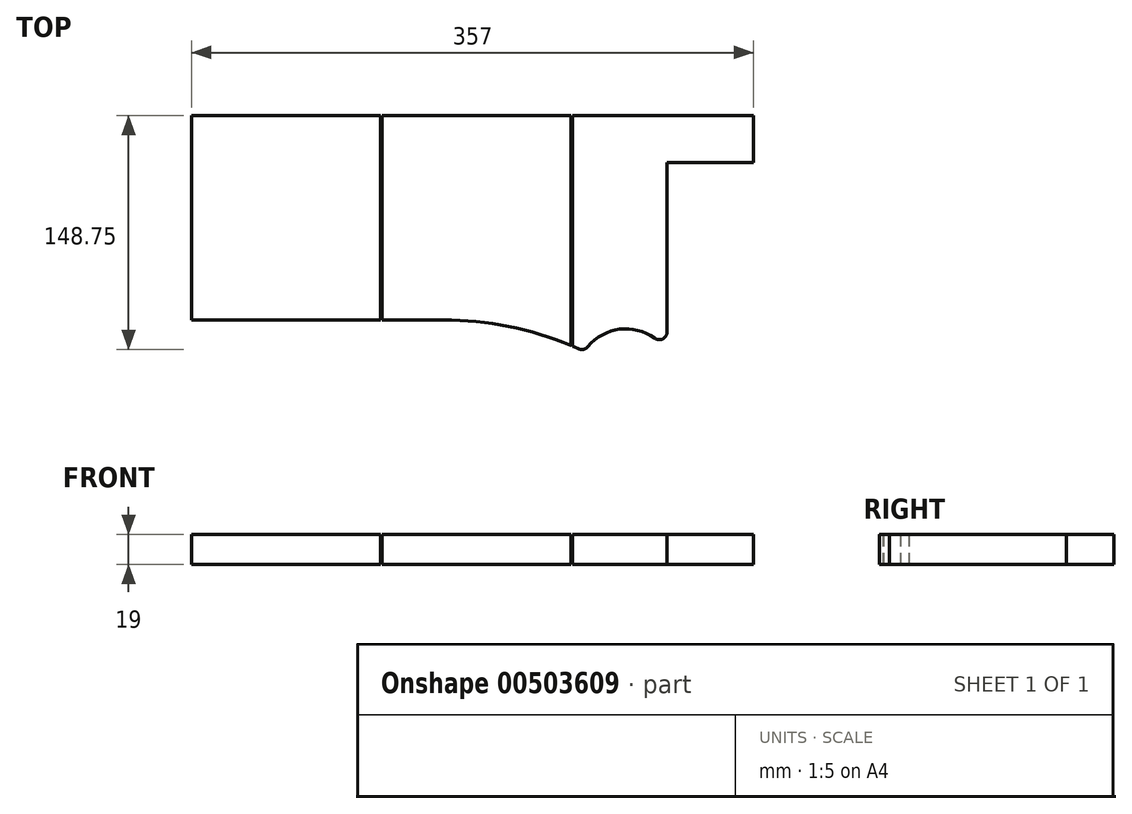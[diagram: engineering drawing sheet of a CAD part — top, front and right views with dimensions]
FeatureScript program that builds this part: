
annotation { "Feature Type Name" : "Feature", "Feature Type Description" : "" }
export const myFeature = defineFeature(function(context is Context, id is Id, definition is map)
    precondition{}
    {
        {
            var Q0;
            Q0=qCreatedBy(makeId("Top.planeOp"),FACE);
            var sketch = newSketch(context, id + "F0", { "sketchPlane" : qUnion([Q0])});
            skLineSegment(sketch, "E0.bottom", {"start": v(-262.8, 99.04) * mm, "end": v(-146.42, 99.04) * mm});
            skLineSegment(sketch, "E0.top", {"start": v(-262.8, -30.96) * mm, "end": v(-102.8, -30.96) * mm});
            skLineSegment(sketch, "E0.left", {"start": v(-262.8, 99.04) * mm, "end": v(-262.8, -30.96) * mm});
            skLineSegment(sketch, "E1", {"start": v(-20.8, -76.9) * mm, "end": v(-21.8, -76.79) * mm});
            skLineSegment(sketch, "E2.trimOffspring", {"start": v(-147.44, 99.04) * mm, "end": v(-40.78, 99.04) * mm});
            skLineSegment(sketch, "E3.bottom", {"start": v(-40.78, 99.04) * mm, "end": v(94.2, 99.04) * mm});
            skLineSegment(sketch, "E3.top", {"start": v(39.2, 69.04) * mm, "end": v(94.2, 69.04) * mm});
            skLineSegment(sketch, "E3.right", {"start": v(94.2, 99.04) * mm, "end": v(94.2, 69.04) * mm});
            skLineSegment(sketch, "E4.bottom", {"start": v(-142.8, 132.48) * mm, "end": v(-141.8, 132.48) * mm});
            skLineSegment(sketch, "E4.top", {"start": v(-142.8, -70.55) * mm, "end": v(-141.8, -70.55) * mm});
            skLineSegment(sketch, "E4.left", {"start": v(-142.8, 132.48) * mm, "end": v(-142.8, -70.55) * mm});
            skLineSegment(sketch, "E4.right", {"start": v(-141.8, 132.48) * mm, "end": v(-141.8, -70.55) * mm});
            skLineSegment(sketch, "E5.bottom", {"start": v(-21.8, 137) * mm, "end": v(-20.8, 137) * mm});
            skLineSegment(sketch, "E5.top", {"start": v(-21.8, -75.06) * mm, "end": v(-20.8, -75.06) * mm});
            skLineSegment(sketch, "E5.left", {"start": v(-21.8, 137) * mm, "end": v(-21.8, -75.06) * mm});
            skLineSegment(sketch, "E5.right", {"start": v(-20.8, 137) * mm, "end": v(-20.8, -75.06) * mm});
            skLineSegment(sketch, "E6.trimOffspring", {"start": v(-141.8, -64.16) * mm, "end": v(-142.8, -64.05) * mm});
            skLineSegment(sketch, "E7", {"start": v(39.2, 69.04) * mm, "end": v(39.2, -38.43) * mm});
            skArc(sketch, "E8", {"start": v(-16.93, -49.28) * mm, "mid": v(-58.9, -35.6) * mm, "end": v(-102.8, -30.96) * mm});
            skArc(sketch, "E9", {"start": v(31.25, -42.47) * mm, "mid": v(9.04, -36.76) * mm, "end": v(-11.03, -47.88) * mm});
            skPoint(sketch, "E10.visualSharp", {"position": v(-13.25, -50.96) * mm});
            skArc(sketch, "E10.filletArc", {"start": v(-16.93, -49.28) * mm, "mid": v(-13.74, -49.58) * mm, "end": v(-11.03, -47.88) * mm});
            skPoint(sketch, "E11.visualSharp", {"position": v(39.2, -50.96) * mm});
            skArc(sketch, "E11.filletArc", {"start": v(31.25, -42.47) * mm, "mid": v(36.46, -42.89) * mm, "end": v(39.2, -38.43) * mm});
            skSolve(sketch);
        }
        {
            var Q0;
            {var subQ5=sQuery(id+"F0.wireOp",EDGE,"E0.bottom");Q0=makeQuery(id+"F0.imprint","IMPRINT",FACE,{"disambiguationData":[TD([[makeQuery(id+"F0.imprint","IMPRINT",EDGE,{"derivedFrom":subQ5}),-1.0]])]});}
            var Q1;
            {var subQ1=sQuery(id+"F0.wireOp",EDGE,"E0.top");var subQ9=sQuery(id+"F0.wireOp",EDGE,"E8");var subQ10=makeQuery(id+"F0.imprint","INTERSECT",VERTEX,{"derivedFrom":[subQ1,subQ9]});Q1=makeQuery(id+"F0.imprint","IMPRINT",FACE,{"disambiguationData":[TD([[makeQuery(id+"F0.imprint","IMPRINT",EDGE,{"disambiguationData":[TD([[subQ10,1.0]])],"derivedFrom":subQ1}),1.0]])]});}
            var Q2;
            Q2=makeQuery(id+"F0.imprint","IMPRINT",FACE,{"disambiguationData":[TD([[makeQuery(id+"F0.imprint","IMPRINT",EDGE,{"derivedFrom":sQuery(id+"F0.wireOp",EDGE,"E3.top")}),1.0]])]});
            extrude(context, id + "F1", {"entities" : qUnion([Q0, Q1, Q2]), "depth" : 19 * mm});
        }
    });
